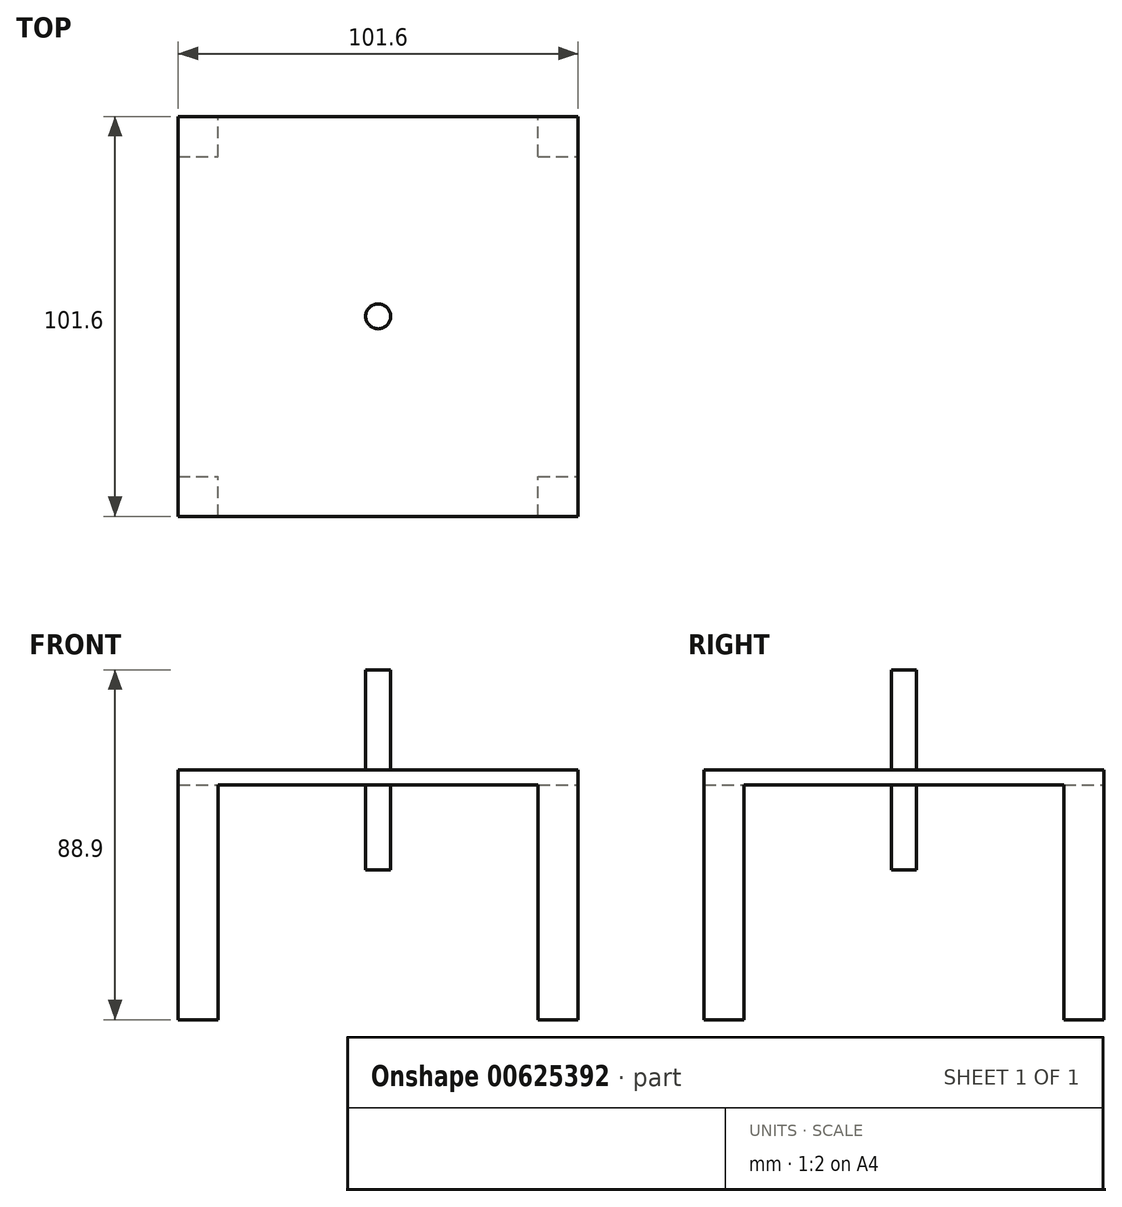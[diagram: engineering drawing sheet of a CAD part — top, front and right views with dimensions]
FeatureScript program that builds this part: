
annotation { "Feature Type Name" : "Feature", "Feature Type Description" : "" }
export const myFeature = defineFeature(function(context is Context, id is Id, definition is map)
    precondition{}
    {
        {
            var Q0;
            Q0=qCreatedBy(makeId("Top.planeOp"),FACE);
            var sketch = newSketch(context, id + "F0", { "sketchPlane" : qUnion([Q0])});
            skLineSegment(sketch, "E0.bottom", {"start": v(0, 0) * mm, "end": v(-101.6, 0) * mm});
            skLineSegment(sketch, "E0.top", {"start": v(0, -101.6) * mm, "end": v(-101.6, -101.6) * mm});
            skLineSegment(sketch, "E0.left", {"start": v(0, 0) * mm, "end": v(0, -101.6) * mm});
            skLineSegment(sketch, "E0.right", {"start": v(-101.6, 0) * mm, "end": v(-101.6, -101.6) * mm});
            skSolve(sketch);
        }
        {
            var Q0;
            Q0 = qSketchRegion(id + "F0", true);
            extrude(context, id + "F1", {"entities" : qUnion([Q0]), "depth" : 63.5 * mm, "offsetDistance" : 25.4 * mm});
        }
        {
            var Q0;
            Q0=makeQuery(id+"F1.opExtrude","CAP_FACE",FACE,{"disambiguationData":[OSD([sQuery(id+"F0.wireOp",EDGE,"E0.bottom"),sQuery(id+"F0.wireOp",EDGE,"E0.top"),sQuery(id+"F0.wireOp",EDGE,"E0.left"),sQuery(id+"F0.wireOp",EDGE,"E0.right")])],"isStart":true});
            var sketch = newSketch(context, id + "F2", { "sketchPlane" : qUnion([Q0])});
            skLineSegment(sketch, "E1.bottom", {"start": v(-110.14, 91.44) * mm, "end": v(13.73, 91.44) * mm});
            skLineSegment(sketch, "E1.top", {"start": v(-110.14, 10.16) * mm, "end": v(13.73, 10.16) * mm});
            skLineSegment(sketch, "E1.left", {"start": v(-110.14, 91.44) * mm, "end": v(-110.14, 10.16) * mm});
            skLineSegment(sketch, "E1.right", {"start": v(13.73, 91.44) * mm, "end": v(13.73, 10.16) * mm});
            skLineSegment(sketch, "E2", {"start": v(-138.08, 101.6) * mm, "end": v(53.38, 101.6) * mm, "construction": true});
            skLineSegment(sketch, "E3", {"start": v(-147.77, 0) * mm, "end": v(62.75, 0) * mm, "construction": true});
            skLineSegment(sketch, "E4.bottom", {"start": v(-91.44, 115.57) * mm, "end": v(-10.16, 115.57) * mm});
            skLineSegment(sketch, "E4.top", {"start": v(-91.44, -18.63) * mm, "end": v(-10.16, -18.63) * mm});
            skLineSegment(sketch, "E4.left", {"start": v(-91.44, 115.57) * mm, "end": v(-91.44, -18.63) * mm});
            skLineSegment(sketch, "E4.right", {"start": v(-10.16, 115.57) * mm, "end": v(-10.16, -18.63) * mm});
            skSolve(sketch);
        }
        {
            var Q0;
            {var subQ0=sQuery(id+"F2.wireOp",EDGE,"E4.left");var subQ1=sQuery(id+"F2.wireOp",EDGE,"E1.bottom");var subQ2=makeQuery(id+"F2.imprint","INTERSECT",VERTEX,{"derivedFrom":[subQ1,subQ0]});Q0=makeQuery(id+"F2.imprint","IMPRINT",FACE,{"disambiguationData":[TD([[makeQuery(id+"F2.imprint","IMPRINT",EDGE,{"disambiguationData":[TD([[subQ2,-1.0]])],"derivedFrom":subQ1}),-1.0]])]});}
            var Q1;
            {var subQ0=sQuery(id+"F2.wireOp",EDGE,"E4.right");var subQ1=sQuery(id+"F2.wireOp",EDGE,"E1.bottom");var subQ2=makeQuery(id+"F2.imprint","INTERSECT",VERTEX,{"derivedFrom":[subQ1,subQ0]});Q1=makeQuery(id+"F2.imprint","IMPRINT",FACE,{"disambiguationData":[TD([[makeQuery(id+"F2.imprint","IMPRINT",EDGE,{"disambiguationData":[TD([[subQ2,-1.0]])],"derivedFrom":subQ1}),-1.0]])]});}
            var Q2;
            {var subQ0=sQuery(id+"F2.wireOp",EDGE,"E4.left");var subQ1=sQuery(id+"F2.wireOp",EDGE,"E1.top");var subQ2=makeQuery(id+"F2.imprint","INTERSECT",VERTEX,{"derivedFrom":[subQ1,subQ0]});Q2=makeQuery(id+"F2.imprint","IMPRINT",FACE,{"disambiguationData":[TD([[makeQuery(id+"F2.imprint","IMPRINT",EDGE,{"disambiguationData":[TD([[subQ2,-1.0]])],"derivedFrom":subQ1}),-1.0]])]});}
            var Q3;
            {var subQ0=sQuery(id+"F2.wireOp",EDGE,"E4.left");var subQ1=sQuery(id+"F2.wireOp",EDGE,"E1.bottom");var subQ2=makeQuery(id+"F2.imprint","INTERSECT",VERTEX,{"derivedFrom":[subQ1,subQ0]});Q3=makeQuery(id+"F2.imprint","IMPRINT",FACE,{"disambiguationData":[TD([[makeQuery(id+"F2.imprint","IMPRINT",EDGE,{"disambiguationData":[TD([[subQ2,1.0]])],"derivedFrom":subQ1}),-1.0]])]});}
            var Q4;
            {var subQ0=sQuery(id+"F2.wireOp",EDGE,"E4.left");var subQ1=sQuery(id+"F2.wireOp",EDGE,"E1.bottom");var subQ2=makeQuery(id+"F2.imprint","INTERSECT",VERTEX,{"derivedFrom":[subQ1,subQ0]});Q4=makeQuery(id+"F2.imprint","IMPRINT",FACE,{"disambiguationData":[TD([[makeQuery(id+"F2.imprint","IMPRINT",EDGE,{"disambiguationData":[TD([[subQ2,-1.0]])],"derivedFrom":subQ1}),1.0]])]});}
            extrude(context, id + "F3", {"entities" : qUnion([Q0, Q1, Q2, Q3, Q4]), "operationType" : NewBodyOperationType.REMOVE, "oppositeDirection" : true, "depth" : 59.69 * mm, "offsetDistance" : 25.4 * mm});
        }
        {
            var Q0;
            Q0=makeQuery(id+"F1.opExtrude","CAP_FACE",FACE,{"disambiguationData":[OSD([sQuery(id+"F0.wireOp",EDGE,"E0.bottom"),sQuery(id+"F0.wireOp",EDGE,"E0.top"),sQuery(id+"F0.wireOp",EDGE,"E0.left"),sQuery(id+"F0.wireOp",EDGE,"E0.right")])],"isStart":false});
            var sketch = newSketch(context, id + "F4", { "sketchPlane" : qUnion([Q0])});
            skLineSegment(sketch, "E5", {"start": v(-101.6, 0) * mm, "end": v(0, -101.6) * mm});
            skCircle(sketch, "E6", {"center": v(-50.8, -50.8) * mm, "radius": 3.17 * mm});
            skSolve(sketch);
        }
        {
            var Q0;
            {var subQ0=sQuery(id+"F4.wireOp",EDGE,"E6");var subQ1=sQuery(id+"F4.wireOp",EDGE,"E5");var subQ2=makeQuery(id+"F4.imprint","INTERSECT",VERTEX,{"disambiguationData":[OD(0.0)],"derivedFrom":[subQ1,subQ0]});Q0=makeQuery(id+"F4.imprint","IMPRINT",FACE,{"disambiguationData":[TD([[makeQuery(id+"F4.imprint","IMPRINT",EDGE,{"disambiguationData":[TD([[subQ2,-1.0]])],"derivedFrom":subQ1}),1.0]])]});}
            var Q1;
            {var subQ0=sQuery(id+"F4.wireOp",EDGE,"E6");var subQ1=sQuery(id+"F4.wireOp",EDGE,"E5");var subQ2=makeQuery(id+"F4.imprint","INTERSECT",VERTEX,{"disambiguationData":[OD(0.0)],"derivedFrom":[subQ1,subQ0]});Q1=makeQuery(id+"F4.imprint","IMPRINT",FACE,{"disambiguationData":[TD([[makeQuery(id+"F4.imprint","IMPRINT",EDGE,{"disambiguationData":[TD([[subQ2,-1.0]])],"derivedFrom":subQ1}),-1.0]])]});}
            extrude(context, id + "F5", {"entities" : qUnion([Q0, Q1]), "operationType" : NewBodyOperationType.REMOVE, "endBound" : BoundingType.THROUGH_ALL, "oppositeDirection" : true, "depth" : 25.4 * mm, "offsetDistance" : 25.4 * mm});
        }
        {
            var Q0;
            Q0=makeQuery(id+"F1.opExtrude","CAP_FACE",FACE,{"disambiguationData":[OSD([sQuery(id+"F0.wireOp",EDGE,"E0.bottom"),sQuery(id+"F0.wireOp",EDGE,"E0.top"),sQuery(id+"F0.wireOp",EDGE,"E0.left"),sQuery(id+"F0.wireOp",EDGE,"E0.right")])],"isStart":false});
            var sketch = newSketch(context, id + "F6", { "sketchPlane" : qUnion([Q0])});
            skCircle(sketch, "E7", {"center": v(-50.8, -50.8) * mm, "radius": 3.18 * mm});
            skSolve(sketch);
        }
        {
            var Q0;
            Q0=makeQuery(id+"F6.imprint","IMPRINT",FACE,{"disambiguationData":[TD([[makeQuery(id+"F6.imprint","IMPRINT",EDGE,{"derivedFrom":sQuery(id+"F6.wireOp",EDGE,"E7")}),1.0]])]});
            extrude(context, id + "F7", {"entities" : qUnion([Q0]), "operationType" : NewBodyOperationType.ADD, "endBound" : BoundingType.SYMMETRIC, "depth" : 50.8 * mm, "offsetDistance" : 25.4 * mm});
        }
    });
